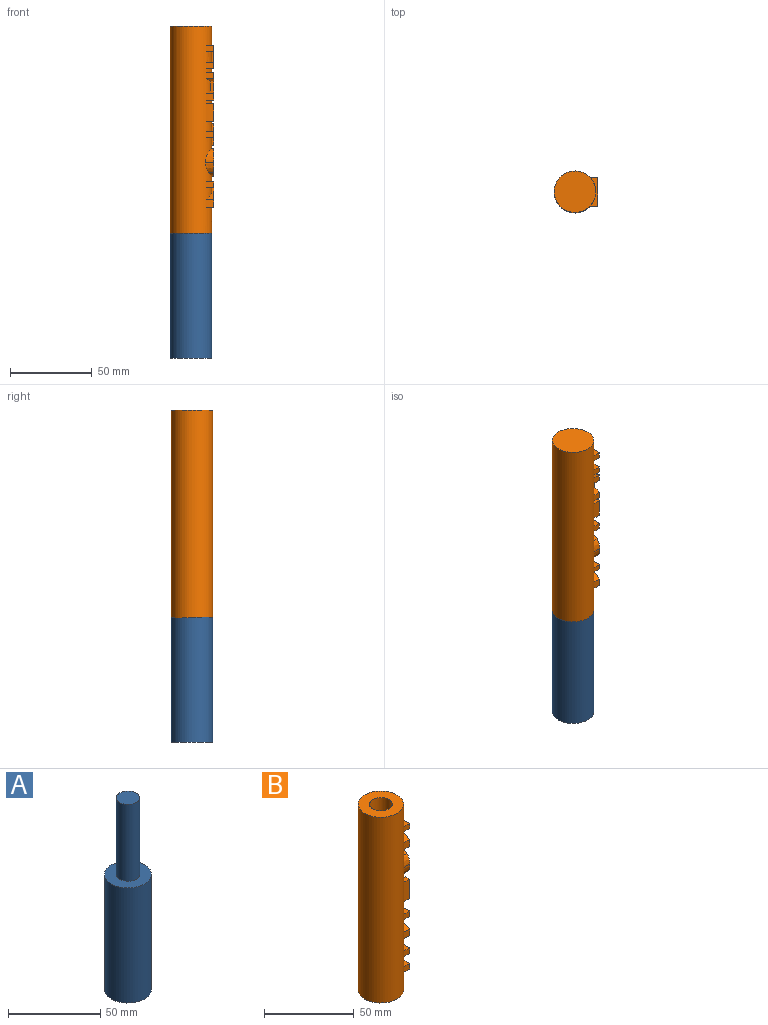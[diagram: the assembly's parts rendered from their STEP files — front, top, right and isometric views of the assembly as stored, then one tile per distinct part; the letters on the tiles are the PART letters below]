
ASSEMBLY  parts=2 mates=1
PART A: 5 faces, bbox 25.4x25.4x127 mm
  f0: plane 25.4x25.4mm, normal (0,0,-1), area 506.7mm2, adj f1
  f1: cylinder r=12.7mm len=76.2mm, axis (0,0,-1), area 6080.5mm2, adj f0,f2
  f2: plane 25.4x25.4mm, normal (0,0,1), area 380mm2, adj f1,f3
  f3: cylinder r=6.35mm len=50.8mm, axis (0,0,-1), area 2026.8mm2, adj f2,f4
  f4: plane 12.7x12.7mm, normal (0,0,1), area 126.7mm2, adj f3
PART B: 79 faces, bbox 26.8x25.5x127.1 mm
  f0: cylinder r=12.7mm len=127mm, axis (0,0,-1), area 9118.6mm2, adj f1,f2,f5,f6,f7,f8,f9,f10
  f1: plane 25.4x25.4mm, normal (0,0,-1), area 506.7mm2, adj f0
  f2: plane 25.4x25.4mm, normal (0,0,1), area 380mm2, adj f0,f3
  f3: cylinder r=6.35mm len=50.8mm, axis (0,0,-1), area 2026.8mm2, adj f2,f4
  f4: plane 12.7x12.7mm, normal (0,0,1), area 126.7mm2, adj f3
  f5: plane 4.71x3.73mm, normal (0,-1,0), area 17.6mm2, adj f0,f6,f16,f17
  f6: plane 6.91x4.71mm, normal (0,0,-1), area 18.1mm2, adj f0,f5,f7,f17
  f7: plane 6.98x1.4mm, normal (0,-1,0), area 9.7mm2, adj f0,f6,f8,f17
  f8: plane 6.91x4.71mm, normal (0,0,1), area 18.1mm2, adj f0,f7,f9,f17
  f9: plane 4.71x3.74mm, normal (0,-1,0), area 17.6mm2, adj f0,f8,f10,f17
  f10: plane 17.63x4.94mm, normal (0,0,-1), area 42mm2, adj f0,f9,f11,f17
  f11: plane 4.94x3.74mm, normal (0,1,0), area 18.5mm2, adj f0,f10,f12,f17
  f12: plane 7.61x4.94mm, normal (0,0,1), area 19.8mm2, adj f0,f11,f13,f17
  f13: plane 6.98x1.34mm, normal (0,1,0), area 9.3mm2, adj f0,f12,f14,f17
  f14: plane 7.61x4.94mm, normal (0,0,-1), area 19.8mm2, adj f0,f13,f15,f17
  f15: plane 4.94x3.73mm, normal (0,1,0), area 18.4mm2, adj f0,f14,f16,f17
  f16: plane 17.63x4.94mm, normal (0,0,1), area 42mm2, adj f0,f5,f15,f17
  f17: plane 17.63x14.45mm, normal (1,0,0), area 153.3mm2, adj f5,f6,f7,f8,f9,f10,f11,f12
  f18: plane 4.94x3.09mm, normal (0,0,1), area 11.4mm2, adj f0,f19,f23,f24
  f19: plane 7.15x2.7mm, normal (0,-1,0), area 19.3mm2, adj f0,f18,f20,f24
  f20: plane 14.54x4.71mm, normal (0,0,1), area 30.6mm2, adj f0,f19,f21,f24
  f21: plane 4.71x3.74mm, normal (0,-1,0), area 17.6mm2, adj f0,f20,f22,f24
  f22: plane 17.63x4.94mm, normal (0,0,-1), area 42mm2, adj f0,f21,f23,f24
  f23: plane 10.89x4.94mm, normal (0,1,0), area 53.8mm2, adj f0,f18,f22,f24
  f24: plane 17.63x10.89mm, normal (1,0,0), area 88mm2, adj f18,f19,f20,f21,f22,f23
  f25: plane 4.78x2.56mm, normal (0,1,0), area 12.3mm2, adj f0,f26,f32,f33
  f26: plane 4.71x3.11mm, normal (0,0,1), area 11mm2, adj f0,f25,f27,f33
  f27: plane 13.31x4.71mm, normal (0,-1,0), area 62.8mm2, adj f0,f26,f28,f33
  f28: plane 4.71x3.11mm, normal (0,0,-1), area 11mm2, adj f0,f27,f29,f33
  f29: plane 4.79x2.56mm, normal (0,1,0), area 12.3mm2, adj f0,f28,f30,f33
  f30: plane 14.52x4.94mm, normal (0,0,-1), area 31mm2, adj f0,f29,f31,f33
  f31: plane 4.94x3.74mm, normal (0,1,0), area 18.5mm2, adj f0,f30,f32,f33
  f32: plane 14.52x4.94mm, normal (0,0,1), area 31mm2, adj f0,f25,f31,f33
  f33: plane 17.63x13.31mm, normal (1,0,0), area 95.7mm2, adj f25,f26,f27,f28,f29,f30,f31,f32
  f34: plane 4.71x3.36mm, normal (0,-1,0), area 15.9mm2, adj f0,f35,f47,f48
  f35: plane 8.35x4.71mm, normal (0,0,-1), area 20mm2, adj f0,f34,f36,f48
  f36: extruded ~4.86x2.1mm, area 8.5mm2, adj f0,f35,f37,f48
  f37: plane 2.1x0.09mm, normal (0,-1,0), area 0.2mm2, adj f0,f36,f38,f48
  f38: plane 13.2x7.66mm, normal (0,-0.5,0.87), area 31.6mm2, adj f0,f37,f39,f48
  f39: plane 4.72x4.71mm, normal (0,-1,0), area 22.2mm2, adj f0,f38,f40,f48
  f40: plane 17.63x4.94mm, normal (0,0,-1), area 42mm2, adj f0,f39,f41,f48
  f41: plane 4.94x3.34mm, normal (0,1,0), area 16.5mm2, adj f0,f40,f42,f48
  f42: plane 8.3x4.94mm, normal (0,0,1), area 20.7mm2, adj f0,f41,f43,f48
  f43: extruded ~5.04x2.06mm, area 8.7mm2, adj f0,f42,f44,f48
  f44: plane 2.06x0.11mm, normal (0,1,0), area 0.2mm2, adj f0,f43,f45,f48
  f45: plane 13.34x7.67mm, normal (0,0.5,-0.87), area 32.6mm2, adj f0,f44,f46,f48
  f46: plane 4.94x4.75mm, normal (0,1,0), area 23.5mm2, adj f0,f45,f47,f48
  f47: plane 17.63x4.94mm, normal (0,0,1), area 42mm2, adj f0,f34,f46,f48
  f48: plane 17.63x15.64mm, normal (1,0,0), area 176.1mm2, adj f34,f35,f36,f37,f38,f39,f40,f41
  f49: extruded ~7.63x2.79mm, area 13.3mm2, adj f50,f60,f61,f62
  f50: extruded ~2.79x1.18mm, area 3mm2, adj f49,f51,f61,f62
  f51: extruded ~6.45x2.23mm, area 10.2mm2, adj f50,f60,f61,f62
  f52: plane 17.7x6.25mm, normal (0,-0.33,0.94), area 44.9mm2, adj f0,f53,f59,f61
  f53: plane 4.78x4.57mm, normal (0,-1,0), area 21.9mm2, adj f0,f52,f54,f61
  f54: plane 17.7x6.22mm, normal (0,-0.33,-0.94), area 44.9mm2, adj f0,f53,f55,f61
  f55: plane 4.94x4.03mm, normal (0,1,0), area 19.9mm2, adj f0,f54,f56,f61
  f56: plane 5.03x4.28mm, normal (0,0.29,0.96), area 14.8mm2, adj f0,f55,f57,f61
  f57: plane 6.43x2.19mm, normal (0,1,0), area 14.1mm2, adj f0,f56,f58,f61
  f58: plane 5.03x4.28mm, normal (0,0.29,-0.96), area 14.8mm2, adj f0,f57,f59,f61
  f59: plane 4.94x4.03mm, normal (0,1,0), area 19.9mm2, adj f0,f52,f58,f61
  f60: plane 4.59x1.37mm, normal (0,-1,0), area 6.3mm2, adj f49,f51,f61,f62
  f61: plane 17.7x17.04mm, normal (1,0,0), area 141.7mm2, adj f49,f50,f51,f52,f53,f54,f55,f56
  f62: cylinder r=12.7mm len=7.63mm, axis (0,0,-1), area 17.9mm2, adj f49,f50,f51,f60
  f63: extruded ~3.36x2.7mm, area 9.1mm2, adj f64,f76,f77,f78
  f64: extruded ~5.95x4.45mm, area 16.4mm2, adj f63,f65,f77,f78
  f65: extruded ~5.95x4.47mm, area 16.8mm2, adj f64,f66,f77,f78
  f66: extruded ~3.35x2.8mm, area 9.4mm2, adj f65,f67,f77,f78
  f67: extruded ~4.45x2.11mm, area 7.7mm2, adj f66,f76,f77,f78
  f68: extruded ~6.22x4.98mm, area 28.1mm2, adj f0,f69,f75,f77
  f69: extruded ~6.24x4.98mm, area 28.2mm2, adj f0,f68,f70,f77
  f70: extruded ~6.72x3.15mm, area 15.6mm2, adj f0,f69,f71,f77
  f71: extruded ~6.75x3.26mm, area 16mm2, adj f0,f70,f72,f77
  f72: extruded ~6.22x5.19mm, area 29.2mm2, adj f0,f71,f73,f77
  f73: extruded ~6.22x5.19mm, area 29.2mm2, adj f0,f72,f74,f77
  f74: extruded ~6.73x3.26mm, area 16mm2, adj f0,f73,f75,f77
  f75: extruded ~6.73x3.14mm, area 15.6mm2, adj f0,f68,f74,f77
  f76: extruded ~4.45x2.04mm, area 7.6mm2, adj f63,f67,f77,f78
  f77: plane 18.15x16.78mm, normal (1,0,0), area 162.8mm2, adj f63,f64,f65,f66,f67,f68,f69,f70
  f78: cylinder r=12.7mm len=11.9mm, axis (0,0,-1), area 86.8mm2, adj f63,f64,f65,f66,f67,f76
PLACE A t=(-44.89,20.11,-13.51)mm
PLACE B rot(axis=(1,0,0),180deg) t=(-44.89,30.34,189.69)mm
MATE slider B.f0 <-> A.f1  axis (0,0,-1) through (-44.89,7.41,62.69)mm
